# Revit family: Plumbing_Fixtures-Oasis-Drinking_Fountain_Barrier_Free-Combo-Split
name_source: partatom
category: Plumbing Fixtures
units: mm (PartAtom-declared; Revit-internal decimal feet)

## family parameters
Cut with Voids When Loaded = No
Host = Face
OmniClass Number = 23.65.70.14.11
OmniClass Title = Drinking Fountains/Coolers
Part Type = Normal
Room Calculation Point = No
Round Connector Dimension = Use Diameter
Shared = No

## types (14) — shared parameters
Accessory Material = Plastic - Oasis International - Gray
Assembly Code = D2010800
CW Connection = Yes
Cold Water Connection Diameter = 0"
Default Elevation = 1' - 1 9/32"
Depth = 1' - 6 5/8"
Flow Rate = 8 GPH
Frequency = 60 Hz
HW Connection = No
Height = 3' - 1 13/16"
Instruction Sheet Link = https://www.oasiscoolers.com
Keynote = 22 40 00.A1
Load Classification = Power
Manufacturer = OASIS International
Manufacturer Fax Number = 1-(614) 322-2529
Product Documentation Link = https://www.oasiscoolers.com
Product Page URL = https://www.oasiscoolers.com
Screen = Screen – Oasis International - Display - Black
URL = https://www.oasiscoolers.com
Vent Connection = No
Version = 2021 - v1.0a
Voltage = 115 V
Voltage Comment = 115 Volts, 60 Hz
Warranty URL = https://www.oasiscoolers.com
Waste Connection = Yes
Waste Water Connection Diameter = 0' - 1 1/4"
Water Pressure = 60.00 psi
Water Pressure Range = 20 - 100 PSI
Width = 2' - 11 1/4"
zero-valued in all types: CWFU, HWFU, WFU

## per-type parameters (varying)
| type | Cabinet Finish | Chilling Option | Description | Filter Option | Finish | Full Load Current | Model | Product Name | Rated Watts | Weight |
| PG8EBFSL-GRY | Paint - Oasis International - Greystone Powder Coated | Delivers 8.0 gallons of chilled drinking water per hour | Refrigerated Fountain | Option to add filtration | Metal - Oasis International - Brushed Stainless Steel | 5 A | PG8EBFSL 507036 | Bi-level Versacooler II W/ Electronic Bottle Filler Versafiller Stainless Steel Alcove, Refrigerated | 500 W | 80.00 lb |
| PGEBFSL-GRY | Paint - Oasis International - Greystone Powder Coated | Non-Refrigerated Fountain | Non-Refrigerated Fountain | Option to add filtration | Metal - Oasis International - Brushed Stainless Steel | 0 A | PGEBFSL 507040 | Bi-level Versacooler II W/ Electronic Bottle Filler Versafiller Stainless Steel Alcove, Non Refrigerated | 11 W | 48.00 lb |
| PGFEBFSL-STL | Metal - Oasis International - Brushed Stainless Steel | Non-Refrigerated Fountain | Non-Refrigerated Fountain | VersaFilter III is Certified to NSF/ANSI 42 and 53 for lead, cyst, Particulate Class I, chlorine, taste and odor reduction to 4,750 gallons | Metal - Oasis International - Brushed Stainless Steel | 0 A | PGFEBFSL 507046 | Bi-level Versacooler II W/ Filtered Electronic Bottle Filler Versafiller Stainless Steel Alcove, Non Refrigerated | 11 W | 50.00 lb |
| PG8FEBFSL-GRY | Paint - Oasis International - Greystone Powder Coated | Delivers 8.0 gallons of chilled drinking water per hour | Refrigerated Fountain | VersaFilter III is Certified to NSF/ANSI 42 and 53 for lead, cyst, Particulate Class I, chlorine, taste and odor reduction to 4,750 gallons | Metal - Oasis International - Brushed Stainless Steel | 5 A | PG8FEBFSL 507043 | Bi-level Versacooler II W/ Filtered Electronic Bottle Filler Versafiller Stainless Steel Alcove, Refrigerated | 500 W | 82.00 lb |
| PGEBFSL-SAN | Metal - Oasis International - Steel Painted Sandstone | Non-Refrigerated Fountain | Non-Refrigerated Fountain | Option to add filtration | Metal - Oasis International - Brushed Stainless Steel | 0 A | PGEBFSL 507041 | Bi-level Versacooler II W/ Electronic Bottle Filler Versafiller Stainless Steel Alcove, Non Refrigerated | 11 W | 48.00 lb |
| PGEBFSL-STL | Metal - Oasis International - Brushed Stainless Steel | Non-Refrigerated Fountain | Non-Refrigerated Fountain | Option to add filtration | Metal - Oasis International - Brushed Stainless Steel | 0 A | PGEBFSL 507042 | Bi-level Versacooler II W/ Electronic Bottle Filler Versafiller Stainless Steel Alcove, Non Refrigerated | 11 W | 48.00 lb |
| PGEBFSL-CHR | Metal - Oasis International - Chrome Plated Brass | Non-Refrigerated Fountain | Non-Refrigerated Fountain | Option to add filtration | Metal - Oasis International - Chrome Plated Brass | 0 A | PGEBFSL 036700-001 | Bi-level Versacooler II W/ Electronic Bottle Filler Versafiller Stainless Steel Alcove, Non Refrigerated | 11 W | 48.00 lb |
| PGFEBFSL-CHR | Metal - Oasis International - Chrome Plated Brass | Non-Refrigerated Fountain | Non-Refrigerated Fountain | VersaFilter III is Certified to NSF/ANSI 42 and 53 for lead, cyst, Particulate Class I, chlorine, taste and odor reduction to 4,750 gallons | Metal - Oasis International - Chrome Plated Brass | 0 A | PGFEBFSL 036700-001 | Bi-level Versacooler II W/ Filtered Electronic Bottle Filler Versafiller Stainless Steel Alcove, Non Refrigerated | 11 W | 50.00 lb |
| PG8EBFSL-SAN | Metal - Oasis International - Steel Painted Sandstone | Delivers 8.0 gallons of chilled drinking water per hour | Refrigerated Fountain | Option to add filtration | Metal - Oasis International - Brushed Stainless Steel | 5 A | PG8EBFSL 507037 | Bi-level Versacooler II W/ Electronic Bottle Filler Versafiller Stainless Steel Alcove, Refrigerated | 500 W | 80.00 lb |
| PG8EBFSL-STL | Metal - Oasis International - Brushed Stainless Steel | Delivers 8.0 gallons of chilled drinking water per hour | Refrigerated Fountain | Option to add filtration | Metal - Oasis International - Brushed Stainless Steel | 5 A | PG8EBFSL 507038 | Bi-level Versacooler II W/ Electronic Bottle Filler Versafiller Stainless Steel Alcove, Refrigerated | 500 W | 80.00 lb |
| PG8EBFSL-CHR | Metal - Oasis International - Chrome Plated Brass | Delivers 8.0 gallons of chilled drinking water per hour | Refrigerated Fountain | Option to add filtration | Metal - Oasis International - Chrome Plated Brass | 5 A | PG8EBFSL 036700-001 | Bi-level Versacooler II W/ Electronic Bottle Filler Versafiller Stainless Steel Alcove, Refrigerated | 500 W | 80.00 lb |
| PG8FEBFSL-SAN | Metal - Oasis International - Steel Painted Sandstone | Delivers 8.0 gallons of chilled drinking water per hour | Refrigerated Fountain | VersaFilter III is Certified to NSF/ANSI 42 and 53 for lead, cyst, Particulate Class I, chlorine, taste and odor reduction to 4,750 gallons | Metal - Oasis International - Brushed Stainless Steel | 5 A | PG8FEBFSL 507044 | Bi-level Versacooler II W/ Filtered Electronic Bottle Filler Versafiller Stainless Steel Alcove, Refrigerated | 500 W | 82.00 lb |
| PG8FEBFSL-STL | Metal - Oasis International - Brushed Stainless Steel | Delivers 8.0 gallons of chilled drinking water per hour | Refrigerated Fountain | VersaFilter III is Certified to NSF/ANSI 42 and 53 for lead, cyst, Particulate Class I, chlorine, taste and odor reduction to 4,750 gallons | Metal - Oasis International - Brushed Stainless Steel | 5 A | PG8FEBFSL 507045 | Bi-level Versacooler II W/ Filtered Electronic Bottle Filler Versafiller Stainless Steel Alcove, Refrigerated | 500 W | 82.00 lb |
| PG8FEBFSL-CHR | Metal - Oasis International - Chrome Plated Brass | Delivers 8.0 gallons of chilled drinking water per hour | Refrigerated Fountain | VersaFilter III is Certified to NSF/ANSI 42 and 53 for lead, cyst, Particulate Class I, chlorine, taste and odor reduction to 4,750 gallons | Metal - Oasis International - Chrome Plated Brass | 5 A | PG8FEBFSL 036700-001 | Bi-level Versacooler II W/ Filtered Electronic Bottle Filler Versafiller Stainless Steel Alcove, Refrigerated | 500 W | 82.00 lb |

## geometry (parser evidence)
native form markers: Sweep x3
no freeform markers — native parametric forms only
